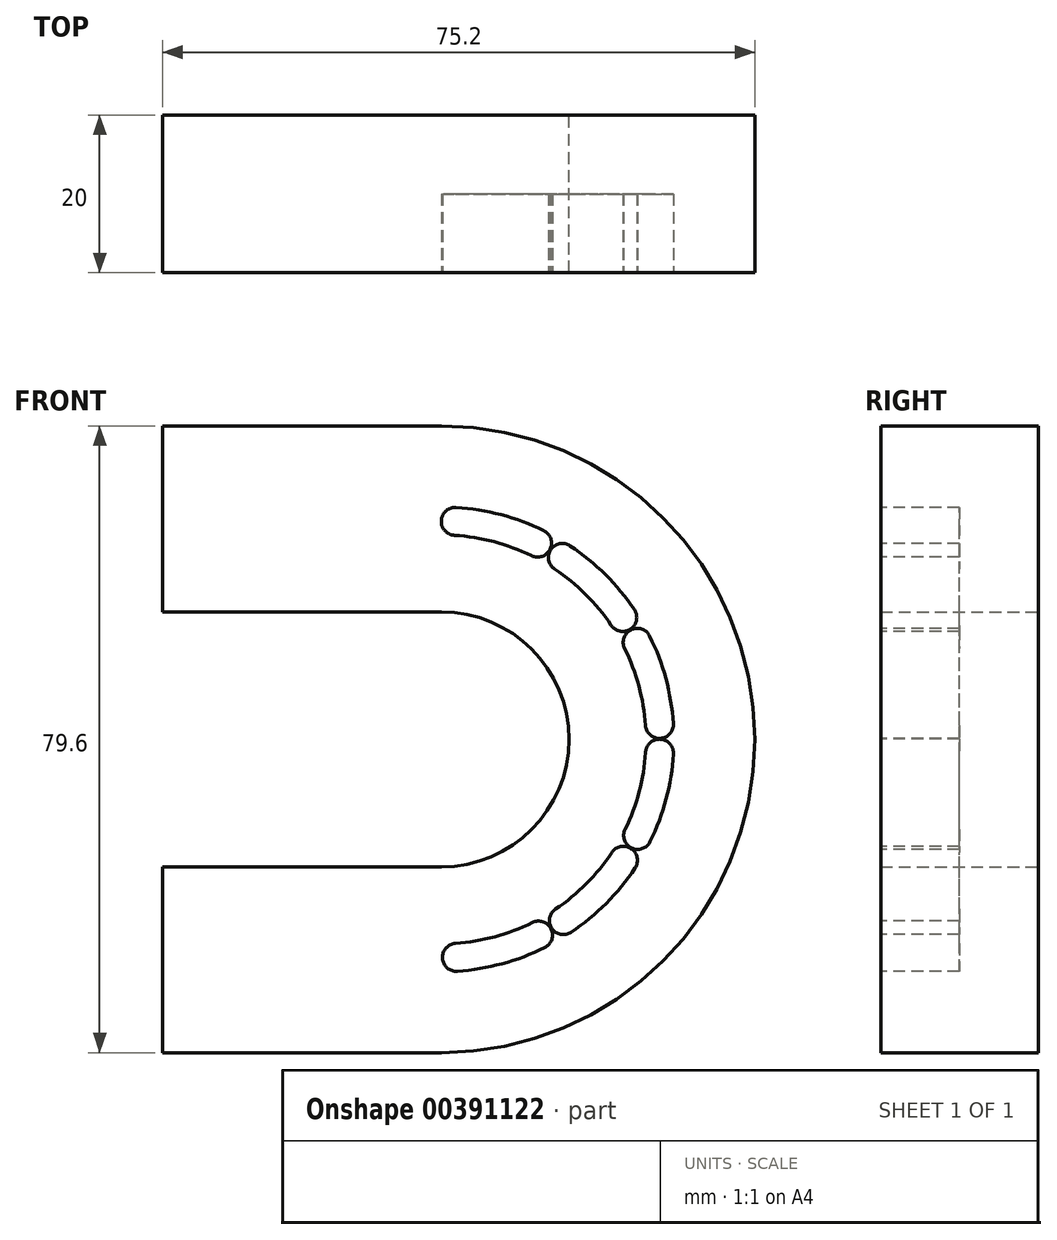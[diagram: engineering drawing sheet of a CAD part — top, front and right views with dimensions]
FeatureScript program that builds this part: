
annotation { "Feature Type Name" : "Feature", "Feature Type Description" : "" }
export const myFeature = defineFeature(function(context is Context, id is Id, definition is map)
    precondition{}
    {
        {
            var Q0;
            Q0=qCreatedBy(makeId("Front.planeOp"),FACE);
            var sketch = newSketch(context, id + "F0", { "sketchPlane" : qUnion([Q0])});
            skLineSegment(sketch, "E0.bottom", {"start": v(0, 39.8) * mm, "end": v(-35.4, 39.8) * mm});
            skLineSegment(sketch, "E0.top", {"start": v(0, -39.8) * mm, "end": v(-35.4, -39.8) * mm});
            skLineSegment(sketch, "E0.right", {"start": v(-35.4, 39.8) * mm, "end": v(-35.4, 16.2) * mm});
            skPoint(sketch, "E0.middle", {"position": v(0, 0) * mm});
            skArc(sketch, "E1", {"start": v(0, -16.2) * mm, "mid": v(16.2, 0) * mm, "end": v(0, 16.2) * mm});
            skLineSegment(sketch, "E2", {"start": v(0, 16.2) * mm, "end": v(-35.4, 16.2) * mm});
            skLineSegment(sketch, "E3", {"start": v(0, -16.2) * mm, "end": v(-35.4, -16.2) * mm});
            skLineSegment(sketch, "E4.trimOffspring", {"start": v(-35.4, -16.2) * mm, "end": v(-35.4, -39.8) * mm});
            skPoint(sketch, "E5.orphan", {"position": v(35.4, 39.8) * mm});
            skPoint(sketch, "E6.orphan", {"position": v(35.4, -39.8) * mm});
            skArc(sketch, "E7", {"start": v(0, -39.8) * mm, "mid": v(39.8, 0) * mm, "end": v(0, 39.8) * mm});
            skLineSegment(sketch, "E8", {"start": v(0, 39.8) * mm, "end": v(0, 16.2) * mm});
            skLineSegment(sketch, "E9.trimOffspring", {"start": v(0, -16.2) * mm, "end": v(0, -39.8) * mm});
            skSolve(sketch);
        }
        {
            var Q0;
            Q0 = qSketchRegion(id + "F0", true);
            extrude(context, id + "F1", {"entities" : qUnion([Q0]), "depth" : 20 * mm});
        }
        {
            var Q0;
            Q0=makeQuery(id+"F1.opExtrude","CAP_FACE",FACE,{"disambiguationData":[OSD([sQuery(id+"F0.wireOp",EDGE,"E0.bottom"),sQuery(id+"F0.wireOp",EDGE,"E0.top"),sQuery(id+"F0.wireOp",EDGE,"E0.right"),sQuery(id+"F0.wireOp",EDGE,"E1"),sQuery(id+"F0.wireOp",EDGE,"E2"),sQuery(id+"F0.wireOp",EDGE,"E3"),sQuery(id+"F0.wireOp",EDGE,"E4.trimOffspring"),sQuery(id+"F0.wireOp",EDGE,"E7")])],"isStart":false});
            var sketch = newSketch(context, id + "F2", { "sketchPlane" : qUnion([Q0])});
            skArc(sketch, "E10", {"start": v(1.86, 29.47) * mm, "mid": v(-0.02, 27.8) * mm, "end": v(1.64, 25.92) * mm});
            skPoint(sketch, "E10.first.point", {"position": v(0, 27.98) * mm});
            skPoint(sketch, "E10.second.point", {"position": v(1.54, 29.46) * mm});
            skPoint(sketch, "E10.third.point", {"position": v(1.36, 25.96) * mm});
            skArc(sketch, "E11.3.0", {"start": v(11.42, 23.33) * mm, "mid": v(13.8, 24.14) * mm, "end": v(12.98, 26.52) * mm});
            skArc(sketch, "E12.trimOffspring", {"start": v(12.98, 26.52) * mm, "mid": v(7.57, 28.54) * mm, "end": v(1.86, 29.47) * mm});
            skArc(sketch, "E13.trimOffspring", {"start": v(11.42, 23.33) * mm, "mid": v(6.66, 25.1) * mm, "end": v(1.64, 25.92) * mm});
            skPoint(sketch, "E14.1.0", {"position": v(16.07, 24.74) * mm});
            skPoint(sketch, "E14.1.1", {"position": v(14, 24.23) * mm});
            skArc(sketch, "E14.1.2", {"start": v(21.56, 14.5) * mm, "mid": v(18.32, 18.42) * mm, "end": v(14.38, 21.63) * mm});
            skPoint(sketch, "E14.1.3", {"position": v(14.16, 21.8) * mm});
            skArc(sketch, "E14.1.4", {"start": v(24.5, 16.48) * mm, "mid": v(20.82, 20.93) * mm, "end": v(16.35, 24.59) * mm});
            skArc(sketch, "E14.1.5", {"start": v(21.56, 14.5) * mm, "mid": v(24.02, 14.01) * mm, "end": v(24.5, 16.48) * mm});
            skArc(sketch, "E14.1.6", {"start": v(16.35, 24.59) * mm, "mid": v(13.89, 24.1) * mm, "end": v(14.38, 21.63) * mm});
            skPoint(sketch, "E14.2.0", {"position": v(26.28, 13.4) * mm});
            skPoint(sketch, "E14.2.1", {"position": v(24.23, 14) * mm});
            skArc(sketch, "E14.2.2", {"start": v(25.92, 1.77) * mm, "mid": v(25.07, 6.79) * mm, "end": v(23.27, 11.54) * mm});
            skPoint(sketch, "E14.2.3", {"position": v(23.17, 11.8) * mm});
            skArc(sketch, "E14.2.4", {"start": v(29.46, 2.02) * mm, "mid": v(28.5, 7.72) * mm, "end": v(26.45, 13.12) * mm});
            skArc(sketch, "E14.2.5", {"start": v(25.92, 1.77) * mm, "mid": v(27.8, 0.12) * mm, "end": v(29.46, 2.02) * mm});
            skArc(sketch, "E14.2.6", {"start": v(26.45, 13.12) * mm, "mid": v(24.07, 13.92) * mm, "end": v(23.27, 11.54) * mm});
            skPoint(sketch, "E14.3.0", {"position": v(29.46, -1.54) * mm});
            skPoint(sketch, "E14.3.1", {"position": v(27.98, 0) * mm});
            skArc(sketch, "E14.3.2", {"start": v(23.33, -11.42) * mm, "mid": v(25.1, -6.66) * mm, "end": v(25.92, -1.64) * mm});
            skPoint(sketch, "E14.3.3", {"position": v(25.96, -1.36) * mm});
            skArc(sketch, "E14.3.4", {"start": v(26.52, -12.98) * mm, "mid": v(28.54, -7.57) * mm, "end": v(29.47, -1.86) * mm});
            skArc(sketch, "E14.3.5", {"start": v(23.33, -11.42) * mm, "mid": v(24.14, -13.8) * mm, "end": v(26.52, -12.98) * mm});
            skArc(sketch, "E14.3.6", {"start": v(29.47, -1.86) * mm, "mid": v(27.8, 0.02) * mm, "end": v(25.92, -1.64) * mm});
            skPoint(sketch, "E14.4.0", {"position": v(24.74, -16.07) * mm});
            skPoint(sketch, "E14.4.1", {"position": v(24.23, -14) * mm});
            skArc(sketch, "E14.4.2", {"start": v(14.5, -21.56) * mm, "mid": v(18.42, -18.32) * mm, "end": v(21.63, -14.38) * mm});
            skPoint(sketch, "E14.4.3", {"position": v(21.8, -14.16) * mm});
            skArc(sketch, "E14.4.4", {"start": v(16.48, -24.5) * mm, "mid": v(20.93, -20.82) * mm, "end": v(24.59, -16.35) * mm});
            skArc(sketch, "E14.4.5", {"start": v(14.5, -21.56) * mm, "mid": v(14.01, -24.02) * mm, "end": v(16.48, -24.5) * mm});
            skArc(sketch, "E14.4.6", {"start": v(24.59, -16.35) * mm, "mid": v(24.1, -13.89) * mm, "end": v(21.63, -14.38) * mm});
            skPoint(sketch, "E14.5.0", {"position": v(13.4, -26.28) * mm});
            skPoint(sketch, "E14.5.1", {"position": v(14, -24.23) * mm});
            skArc(sketch, "E14.5.2", {"start": v(1.77, -25.92) * mm, "mid": v(6.79, -25.07) * mm, "end": v(11.54, -23.27) * mm});
            skPoint(sketch, "E14.5.3", {"position": v(11.8, -23.17) * mm});
            skArc(sketch, "E14.5.4", {"start": v(2.02, -29.46) * mm, "mid": v(7.72, -28.5) * mm, "end": v(13.12, -26.45) * mm});
            skArc(sketch, "E14.5.5", {"start": v(1.77, -25.92) * mm, "mid": v(0.12, -27.8) * mm, "end": v(2.02, -29.46) * mm});
            skArc(sketch, "E14.5.6", {"start": v(13.12, -26.45) * mm, "mid": v(13.92, -24.07) * mm, "end": v(11.54, -23.27) * mm});
            skLineSegment(sketch, "E14.anchor1", {"start": v(0, 0) * mm, "end": v(1.36, 25.96) * mm, "construction": true});
            skLineSegment(sketch, "E14.anchor2", {"start": v(0, 0) * mm, "end": v(11.8, -23.17) * mm, "construction": true});
            skSolve(sketch);
        }
        {
            var Q0;
            Q0 = qSketchRegion(id + "F2", true);
            extrude(context, id + "F3", {"entities" : qUnion([Q0]), "operationType" : NewBodyOperationType.REMOVE, "oppositeDirection" : true, "depth" : 10 * mm});
        }
    });
